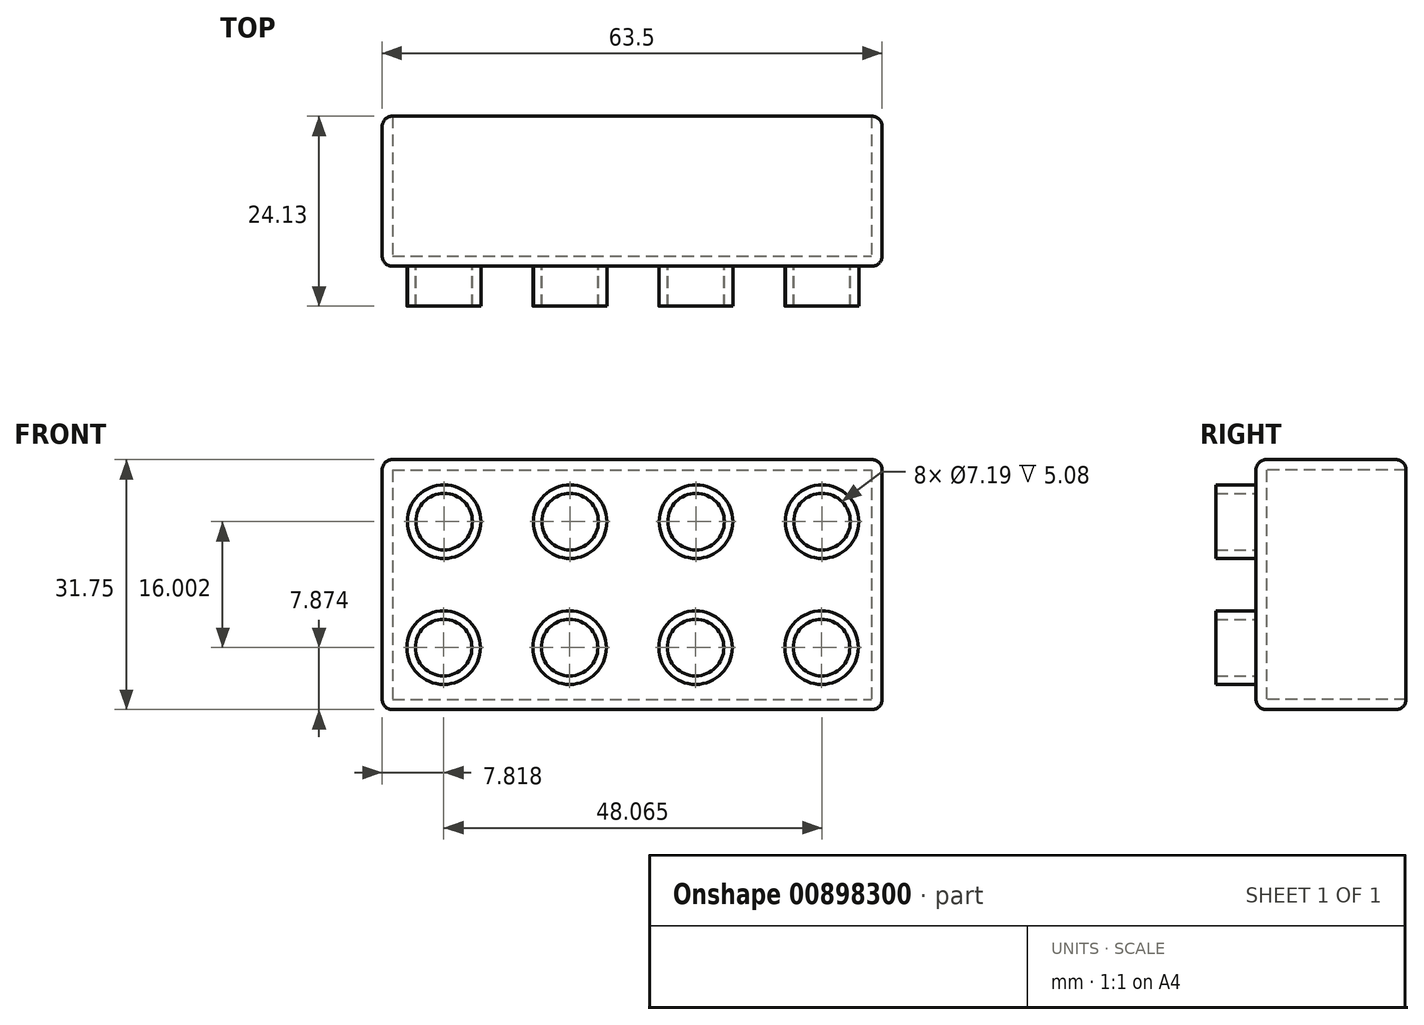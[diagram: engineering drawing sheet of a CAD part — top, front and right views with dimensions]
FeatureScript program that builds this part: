
annotation { "Feature Type Name" : "Feature", "Feature Type Description" : "" }
export const myFeature = defineFeature(function(context is Context, id is Id, definition is map)
    precondition{}
    {
        {
            var Q0;
            Q0=qCreatedBy(makeId("Top.planeOp"),FACE);
            var sketch = newSketch(context, id + "F0", { "sketchPlane" : qUnion([Q0])});
            skLineSegment(sketch, "E0.bottom", {"start": v(-57.87, 31.18) * mm, "end": v(5.63, 31.18) * mm});
            skLineSegment(sketch, "E0.top", {"start": v(-57.87, 12.13) * mm, "end": v(5.63, 12.13) * mm});
            skLineSegment(sketch, "E0.left", {"start": v(-57.87, 31.18) * mm, "end": v(-57.87, 12.13) * mm});
            skLineSegment(sketch, "E0.right", {"start": v(5.63, 31.18) * mm, "end": v(5.63, 12.13) * mm});
            skSolve(sketch);
        }
        {
            var Q0;
            Q0=makeQuery(id+"F0.imprint","IMPRINT",FACE,{"disambiguationData":[TD([[makeQuery(id+"F0.imprint","IMPRINT",EDGE,{"derivedFrom":sQuery(id+"F0.wireOp",EDGE,"E0.bottom")}),-1.0]])]});
            extrude(context, id + "F1", {"entities" : qUnion([Q0]), "depth" : 31.75 * mm, "offsetDistance" : 25.4 * mm});
        }
        {
            var Q0;
            Q0=makeQuery(id+"F1.opExtrude","SWEPT_FACE",FACE,{"disambiguationData":[OSD([sQuery(id+"F0.wireOp",EDGE,"E0.bottom")])]});
            shell(context, id + "F2", {"entities" : qUnion([Q0]), "thickness" : 1.32 * mm});
        }
        {
            var Q0;
            Q0=makeQuery(id+"F1.opExtrude","SWEPT_FACE",FACE,{"disambiguationData":[OSD([sQuery(id+"F0.wireOp",EDGE,"E0.top")])]});
            var sketch = newSketch(context, id + "F3", { "sketchPlane" : qUnion([Q0])});
            skCircle(sketch, "E1", {"center": v(-50, 23.88) * mm, "radius": 4.67 * mm});
            skCircle(sketch, "E2", {"center": v(-50, 23.88) * mm, "radius": 3.6 * mm});
            skCircle(sketch, "E3.1.0.0", {"center": v(-34, 23.88) * mm, "radius": 4.67 * mm});
            skCircle(sketch, "E3.1.0.1", {"center": v(-34, 23.88) * mm, "radius": 3.6 * mm});
            skCircle(sketch, "E3.2.0.0", {"center": v(-17.99, 23.88) * mm, "radius": 4.67 * mm});
            skCircle(sketch, "E3.2.0.1", {"center": v(-17.99, 23.88) * mm, "radius": 3.6 * mm});
            skCircle(sketch, "E3.3.0.0", {"center": v(-1.99, 23.88) * mm, "radius": 4.67 * mm});
            skCircle(sketch, "E3.3.0.1", {"center": v(-1.99, 23.88) * mm, "radius": 3.6 * mm});
            skLineSegment(sketch, "E3.direction1", {"start": v(-50, 23.88) * mm, "end": v(-34, 23.88) * mm, "construction": true});
            skCircle(sketch, "E4.1.0.0", {"center": v(-50.05, 7.87) * mm, "radius": 3.6 * mm});
            skCircle(sketch, "E4.1.0.1", {"center": v(-50.05, 7.87) * mm, "radius": 4.67 * mm});
            skCircle(sketch, "E4.1.0.2", {"center": v(-34.05, 7.87) * mm, "radius": 4.67 * mm});
            skCircle(sketch, "E4.1.0.3", {"center": v(-34.05, 7.87) * mm, "radius": 3.6 * mm});
            skCircle(sketch, "E4.1.0.4", {"center": v(-18.05, 7.87) * mm, "radius": 4.67 * mm});
            skCircle(sketch, "E4.1.0.5", {"center": v(-18.05, 7.87) * mm, "radius": 3.6 * mm});
            skCircle(sketch, "E4.1.0.6", {"center": v(-2.05, 7.87) * mm, "radius": 4.67 * mm});
            skCircle(sketch, "E4.1.0.7", {"center": v(-2.05, 7.87) * mm, "radius": 3.6 * mm});
            skLineSegment(sketch, "E4.direction1", {"start": v(-50, 23.88) * mm, "end": v(-50.05, 7.87) * mm, "construction": true});
            skSolve(sketch);
        }
        {
            var Q0;
            Q0 = qSketchRegion(id + "F3", true);
            extrude(context, id + "F4", {"entities" : qUnion([Q0]), "operationType" : NewBodyOperationType.ADD, "depth" : 5.08 * mm, "offsetDistance" : 25.4 * mm});
        }
        {
            var Q0;
            Q0=makeQuery(id+"F1.opExtrude","CAP_FACE",FACE,{"disambiguationData":[OSD([sQuery(id+"F0.wireOp",EDGE,"E0.bottom"),sQuery(id+"F0.wireOp",EDGE,"E0.top"),sQuery(id+"F0.wireOp",EDGE,"E0.left"),sQuery(id+"F0.wireOp",EDGE,"E0.right")])],"isStart":true});
            var Q1;
            Q1=makeQuery(id+"F1.opExtrude","SWEPT_FACE",FACE,{"disambiguationData":[OSD([sQuery(id+"F0.wireOp",EDGE,"E0.left")])]});
            var Q2;
            Q2=makeQuery(id+"F1.opExtrude","CAP_FACE",FACE,{"disambiguationData":[OSD([sQuery(id+"F0.wireOp",EDGE,"E0.bottom"),sQuery(id+"F0.wireOp",EDGE,"E0.top"),sQuery(id+"F0.wireOp",EDGE,"E0.left"),sQuery(id+"F0.wireOp",EDGE,"E0.right")])],"isStart":false});
            var Q3;
            Q3=makeQuery(id+"F1.opExtrude","SWEPT_FACE",FACE,{"disambiguationData":[OSD([sQuery(id+"F0.wireOp",EDGE,"E0.right")])]});
            fillet(context, id + "F5", {"entities" : qUnion([Q0, Q1, Q2, Q3]), "radius" : 1.27 * mm, "tangentPropagation" : true, "allowEdgeOverflow" : false});
        }
    });
